# Revit family: Bayville Spike Spot 12V
name_source: partatom
category: Lighting Fixtures
revit_build: Autodesk Revit 2018 (Build: 20170223_1515(x64)
units: mm (PartAtom-declared; Revit-internal decimal feet)

## family parameters
Always vertical = Yes
Cut with Voids When Loaded = No
Light Source = Yes
OmniClass Number = 23.80.70.00
OmniClass Title = Lighting
Part Type = Normal
Room Calculation Point = No
Round Connector Dimension = Use Diameter
Shared = No
Work Plane-Based = No

## types (2) — shared parameters
Color Filter = 16777215
Dimmable = Yes - Driver Dependent
Dimming Lamp Color Temperature Shift = <None>
Dimming Method = Driver Dependent
Dims MM = 94 x 75 x 102
Efficacy (lm/W) = 65
Electrical Class = 3
Emit from Line Length = 610 mm
Lamp = LED
Length of Cable Supplied = 1300
Location Rating = IP65
Main Material = Aluminium / Stainless steel Spike
Photometric Web File = 1401009_Bayville Spike Spot 12V_Photometry_IES_Iss. 01.ies
Power (W) = 6.5 W ( inc driver )
Product Location = Ground
Product Name = Bayville Spike Spot
Product URL = https://www.astrolighting.com
Tilt Angle = 60.00°
Weight KG = 0.87

## per-type parameters (varying)
| type | Driver Required | Main Finish | Product SKU |
| Astro Bayville Spike 12V - Textured Black | yes 12V | Textured black | 1401009 |
| Astro Bayville Spike 12V - Textured Grey | Yes - 12V | Textured Grey | 1401010 |

## geometry (parser evidence)
native form markers: Sweep x2
no freeform markers — native parametric forms only
